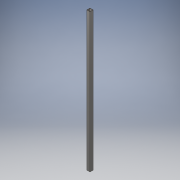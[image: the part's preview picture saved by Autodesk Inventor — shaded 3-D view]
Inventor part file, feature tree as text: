
AUTODESK INVENTOR PART (.ipt)
format: ipt  version: 2019 (Build 230136000, 136)  size: 101,376 bytes
history: native  units: mm
features: extrude x1, sketch x1
ambient origin geometry x8: Origin, YZ Plane, XZ Plane, XY Plane, X Axis, Y Axis, Z Axis, Center Point
bodies: Solid1 (feature_tree)
feature tree (2):
  extrude  "Extrusion1"  Depth=30.0mm
  sketch  "Sketch1"  dims[d0=30.0mm d1=30.0mm d2=2.5mm d3=2.5mm d4=1250.0mm d5=0.0mm]
